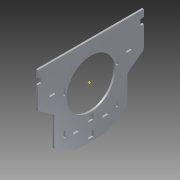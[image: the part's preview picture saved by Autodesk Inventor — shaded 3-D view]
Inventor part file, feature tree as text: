
AUTODESK INVENTOR PART (.ipt)
format: ipt  version: 2015 (Build 190159000, 159)  size: 241,152 bytes
history: native  units: mm
features: extrude x1, sketch x1
ambient origin geometry x8: Origin, YZ Plane, XZ Plane, XY Plane, X Axis, Y Axis, Z Axis, Center Point
bodies: Body1 (feature_tree)
feature tree (2):
  extrude  "Extrusion6"  Depth=6.0mm
  sketch  "Sketch2"  dims[d8=0.0mm d21=6.0mm d22=10.0mm d25=6.0mm d26=10.0mm d31=3.0mm d32=10.0mm d35=3.0mm d36=10.0mm d39=25.0mm d40=25.0mm d43=82.55mm d52=3.0mm d53=10.0mm d54=10.0mm d55=3.0mm d58=10.0mm d59=3.0mm d62=3.0mm d65=180.0mm d69=20.0mm d71=20.0mm d72=43.5mm d73=43.5mm d74=60.0mm d75=60.0mm d76=10.0mm d77=10.0mm d78=60.0mm d79=90.0mm d80=43.5mm d81=43.5mm d87=15.0mm d90=90.0mm d91=90.0mm d103=10.0mm d104=10.0mm d108=3.0mm d109=10.0mm d110=20.0mm d111=3.0mm d112=10.0mm d113=20.0mm d114=5.0mm d115=10.0mm d116=9.0mm d117=4.5mm d118=10.0mm d119=9.0mm d120=15.0mm d121=4.5mm d124=3.0mm d125=0.0mm d127=180.0mm d128=150.0mm d130=85.5mm d131=43.5mm d132=43.5mm d133=60.0mm d134=60.0mm d135=43.5mm d136=43.5mm d137=90.0deg d138=28.0mm d140=47.0mm d141=47.0mm d144=60.0mm d145=20.0mm d147=65.0mm d149=50.0mm d151=10.0mm d152=60.0mm d153=20.0mm d154=50.0mm d155=62.0mm d156=62.0mm d157=62.0mm d158=57.0mm d159=57.0mm d160=3.0mm d161=24.0mm d162=24.0mm d163=90.0mm d164=5.0mm]
